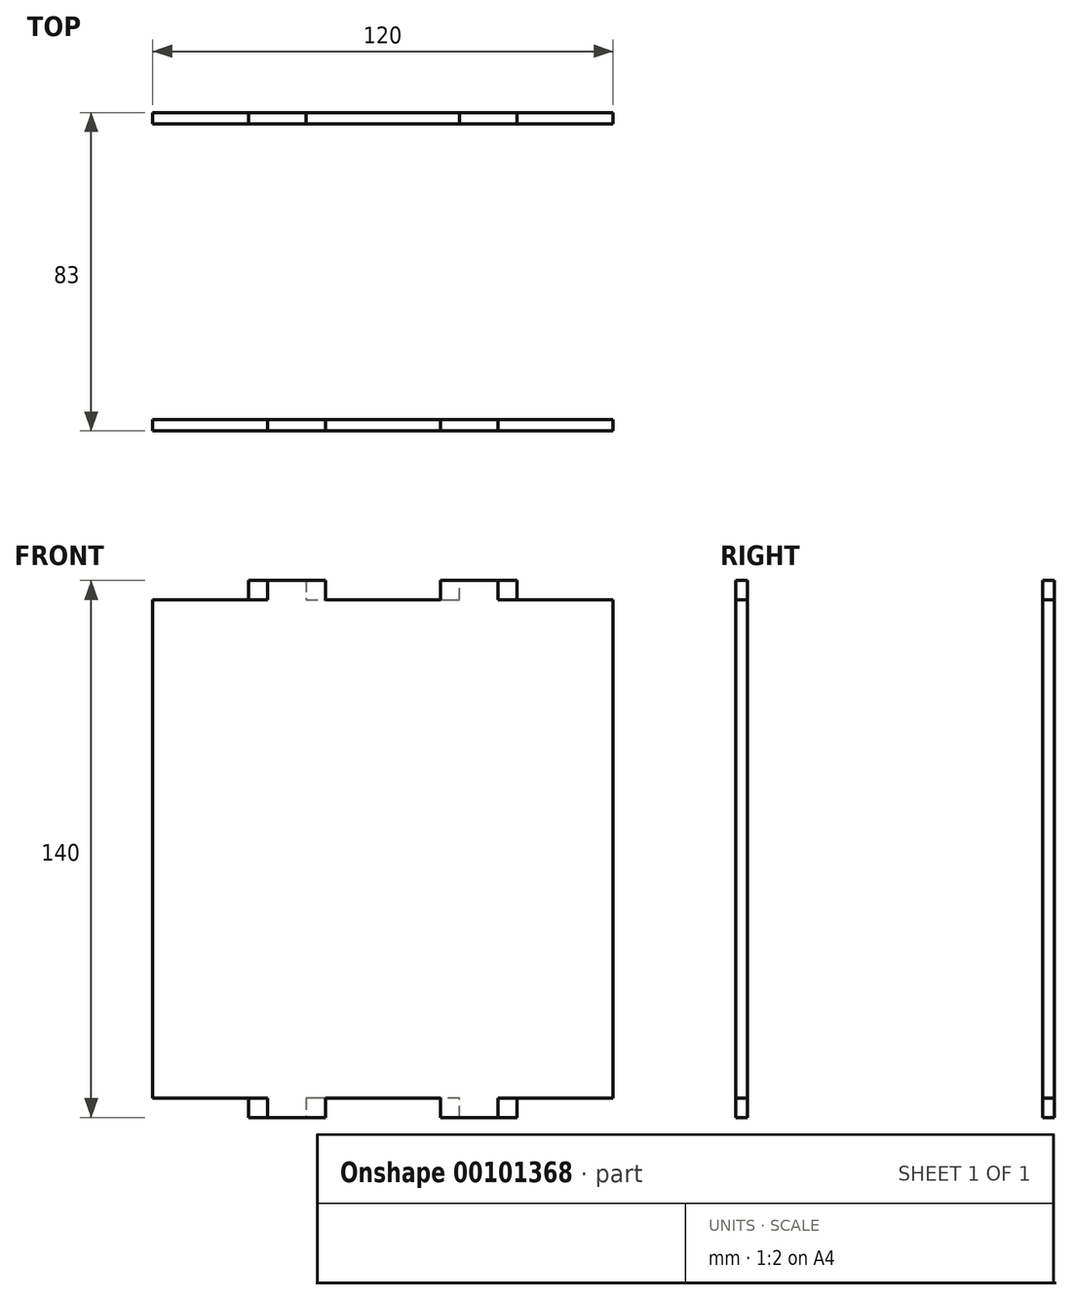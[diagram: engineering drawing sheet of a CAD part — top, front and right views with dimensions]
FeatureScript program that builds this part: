
annotation { "Feature Type Name" : "Feature", "Feature Type Description" : "" }
export const myFeature = defineFeature(function(context is Context, id is Id, definition is map)
    precondition{}
    {
        {
            var Q0;
            Q0=qCreatedBy(makeId("Front.planeOp"),FACE);
            var sketch = newSketch(context, id + "F0", { "sketchPlane" : qUnion([Q0])});
            skLineSegment(sketch, "E0", {"start": v(-60, 65) * mm, "end": v(-35, 65) * mm});
            skLineSegment(sketch, "E1", {"start": v(-35, 65) * mm, "end": v(-35, 70) * mm});
            skLineSegment(sketch, "E2", {"start": v(-35, 70) * mm, "end": v(-20, 70) * mm});
            skLineSegment(sketch, "E3", {"start": v(-20, 70) * mm, "end": v(-20, 65) * mm});
            skLineSegment(sketch, "E4", {"start": v(-20, 65) * mm, "end": v(20, 65) * mm});
            skLineSegment(sketch, "E5", {"start": v(20, 65) * mm, "end": v(20, 70) * mm});
            skLineSegment(sketch, "E6", {"start": v(20, 70) * mm, "end": v(35, 70) * mm});
            skLineSegment(sketch, "E7", {"start": v(35, 70) * mm, "end": v(35, 65) * mm});
            skLineSegment(sketch, "E8", {"start": v(35, 65) * mm, "end": v(60, 65) * mm});
            skLineSegment(sketch, "E9", {"start": v(60, 65) * mm, "end": v(60, -65) * mm});
            skLineSegment(sketch, "E10", {"start": v(60, -65) * mm, "end": v(35, -65) * mm});
            skLineSegment(sketch, "E11", {"start": v(35, -65) * mm, "end": v(35, -70) * mm});
            skLineSegment(sketch, "E12", {"start": v(35, -70) * mm, "end": v(20, -70) * mm});
            skLineSegment(sketch, "E13", {"start": v(20, -70) * mm, "end": v(20, -65) * mm});
            skLineSegment(sketch, "E14", {"start": v(20, -65) * mm, "end": v(-20, -65) * mm});
            skLineSegment(sketch, "E15", {"start": v(-20, -65) * mm, "end": v(-20, -70) * mm});
            skLineSegment(sketch, "E16", {"start": v(-20, -70) * mm, "end": v(-35, -70) * mm});
            skLineSegment(sketch, "E17", {"start": v(-35, -70) * mm, "end": v(-35, -65) * mm});
            skLineSegment(sketch, "E18", {"start": v(-35, -65) * mm, "end": v(-60, -65) * mm});
            skLineSegment(sketch, "E19", {"start": v(-60, -65) * mm, "end": v(-60, 65) * mm});
            skPoint(sketch, "E20", {"position": v(-60, 0) * mm});
            skLineSegment(sketch, "E21", {"start": v(-60, 0) * mm, "end": v(60, 0) * mm, "construction": true});
            skPoint(sketch, "E22", {"position": v(0, 0) * mm});
            skSolve(sketch);
        }
        {
            var Q0;
            Q0=makeQuery(id+"F0.imprint","IMPRINT",FACE,{"disambiguationData":[TD([[makeQuery(id+"F0.imprint","IMPRINT",EDGE,{"derivedFrom":sQuery(id+"F0.wireOp",EDGE,"E0")}),-1.0]])]});
            extrude(context, id + "F1", {"entities" : qUnion([Q0]), "depth" : 3 * mm});
        }
        {
            var Q0;
            Q0=qCreatedBy(makeId("Front.planeOp"),FACE);
            cPlane(context, id + "F2", {"entities" : qUnion([Q0]), "cplaneType" : CPlaneType.OFFSET, "offset" : 80 * mm, "width" : 150 * mm, "height" : 150 * mm});
        }
        {
            var Q0;
            Q0=qCreatedBy(id+"F2.planeOp",FACE);
            var sketch = newSketch(context, id + "F3", { "sketchPlane" : qUnion([Q0])});
            skLineSegment(sketch, "E23", {"start": v(-60, 65) * mm, "end": v(-30, 65) * mm});
            skLineSegment(sketch, "E24", {"start": v(-30, 65) * mm, "end": v(-30, 70) * mm});
            skLineSegment(sketch, "E25", {"start": v(-30, 70) * mm, "end": v(-15, 70) * mm});
            skLineSegment(sketch, "E26", {"start": v(-15, 70) * mm, "end": v(-15, 65) * mm});
            skLineSegment(sketch, "E27", {"start": v(-15, 65) * mm, "end": v(15, 65) * mm});
            skLineSegment(sketch, "E28", {"start": v(15, 65) * mm, "end": v(15, 70) * mm});
            skLineSegment(sketch, "E29", {"start": v(15, 70) * mm, "end": v(30, 70) * mm});
            skLineSegment(sketch, "E30", {"start": v(30, 70) * mm, "end": v(30, 65) * mm});
            skLineSegment(sketch, "E31", {"start": v(30, 65) * mm, "end": v(60, 65) * mm});
            skLineSegment(sketch, "E32", {"start": v(60, 65) * mm, "end": v(60, -65) * mm});
            skLineSegment(sketch, "E33", {"start": v(60, -65) * mm, "end": v(30, -65) * mm});
            skLineSegment(sketch, "E34", {"start": v(30, -65) * mm, "end": v(30, -70) * mm});
            skLineSegment(sketch, "E35", {"start": v(30, -70) * mm, "end": v(15, -70) * mm});
            skLineSegment(sketch, "E36", {"start": v(15, -70) * mm, "end": v(15, -65) * mm});
            skLineSegment(sketch, "E37", {"start": v(15, -65) * mm, "end": v(-15, -65) * mm});
            skLineSegment(sketch, "E38", {"start": v(-15, -65) * mm, "end": v(-15, -70) * mm});
            skLineSegment(sketch, "E39", {"start": v(-15, -70) * mm, "end": v(-30, -70) * mm});
            skLineSegment(sketch, "E40", {"start": v(-30, -70) * mm, "end": v(-30, -65) * mm});
            skLineSegment(sketch, "E41", {"start": v(-30, -65) * mm, "end": v(-60, -65) * mm});
            skLineSegment(sketch, "E42", {"start": v(-60, -65) * mm, "end": v(-60, 65) * mm});
            skPoint(sketch, "E43", {"position": v(-60, 0) * mm});
            skLineSegment(sketch, "E44", {"start": v(-60, 0) * mm, "end": v(60, 0) * mm, "construction": true});
            skPoint(sketch, "E45", {"position": v(0, 0) * mm});
            skSolve(sketch);
        }
        {
            var Q0;
            Q0=makeQuery(id+"F3.imprint","IMPRINT",FACE,{"disambiguationData":[TD([[makeQuery(id+"F3.imprint","IMPRINT",EDGE,{"derivedFrom":sQuery(id+"F3.wireOp",EDGE,"E23")}),-1.0]])]});
            extrude(context, id + "F4", {"entities" : qUnion([Q0]), "depth" : 3 * mm});
        }
    });
